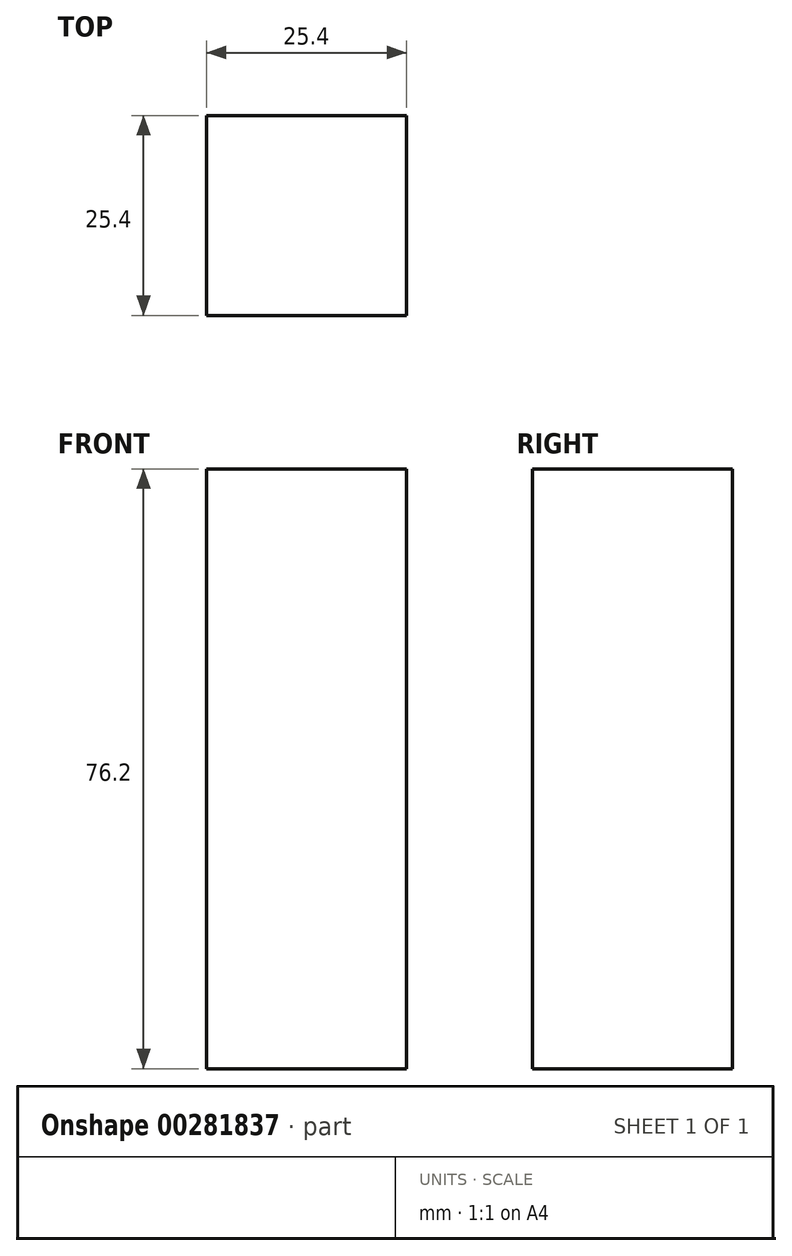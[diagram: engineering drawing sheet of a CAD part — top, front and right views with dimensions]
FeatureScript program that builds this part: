
annotation { "Feature Type Name" : "Feature", "Feature Type Description" : "" }
export const myFeature = defineFeature(function(context is Context, id is Id, definition is map)
    precondition{}
    {
        {
            var Q0;
            Q0=qCreatedBy(makeId("Front.planeOp"),FACE);
            var sketch = newSketch(context, id + "F0", { "sketchPlane" : qUnion([Q0])});
            skLineSegment(sketch, "E0.bottom", {"start": v(-61.5, 124.32) * mm, "end": v(-36.1, 124.32) * mm});
            skLineSegment(sketch, "E0.top", {"start": v(-61.5, 48.12) * mm, "end": v(-36.1, 48.12) * mm});
            skLineSegment(sketch, "E0.left", {"start": v(-61.5, 124.32) * mm, "end": v(-61.5, 48.12) * mm});
            skLineSegment(sketch, "E0.right", {"start": v(-36.1, 124.32) * mm, "end": v(-36.1, 48.12) * mm});
            skSolve(sketch);
        }
        {
            var Q0;
            Q0 = qSketchRegion(id + "F0", true);
            extrude(context, id + "F1", {"entities" : qUnion([Q0]), "depth" : 25.4 * mm});
        }
    });
